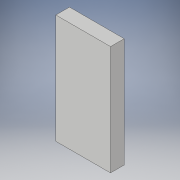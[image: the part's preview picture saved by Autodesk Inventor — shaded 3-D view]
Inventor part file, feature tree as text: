
AUTODESK INVENTOR PART (.ipt)
format: ipt  version: 2019 (Build 230136000, 136)  size: 94,720 bytes
history: native  units: mm
features: other x1, extrude x1, sketch x1
ambient origin geometry x8: Origin, YZ Plane, XZ Plane, XY Plane, X Axis, Y Axis, Z Axis, Center Point
bodies: Body1 (feature_tree)
feature tree (3):
  other  "ソリッド1"
  extrude  "押し出し1"  Depth=40.0mm
  sketch  "スケッチ1"
